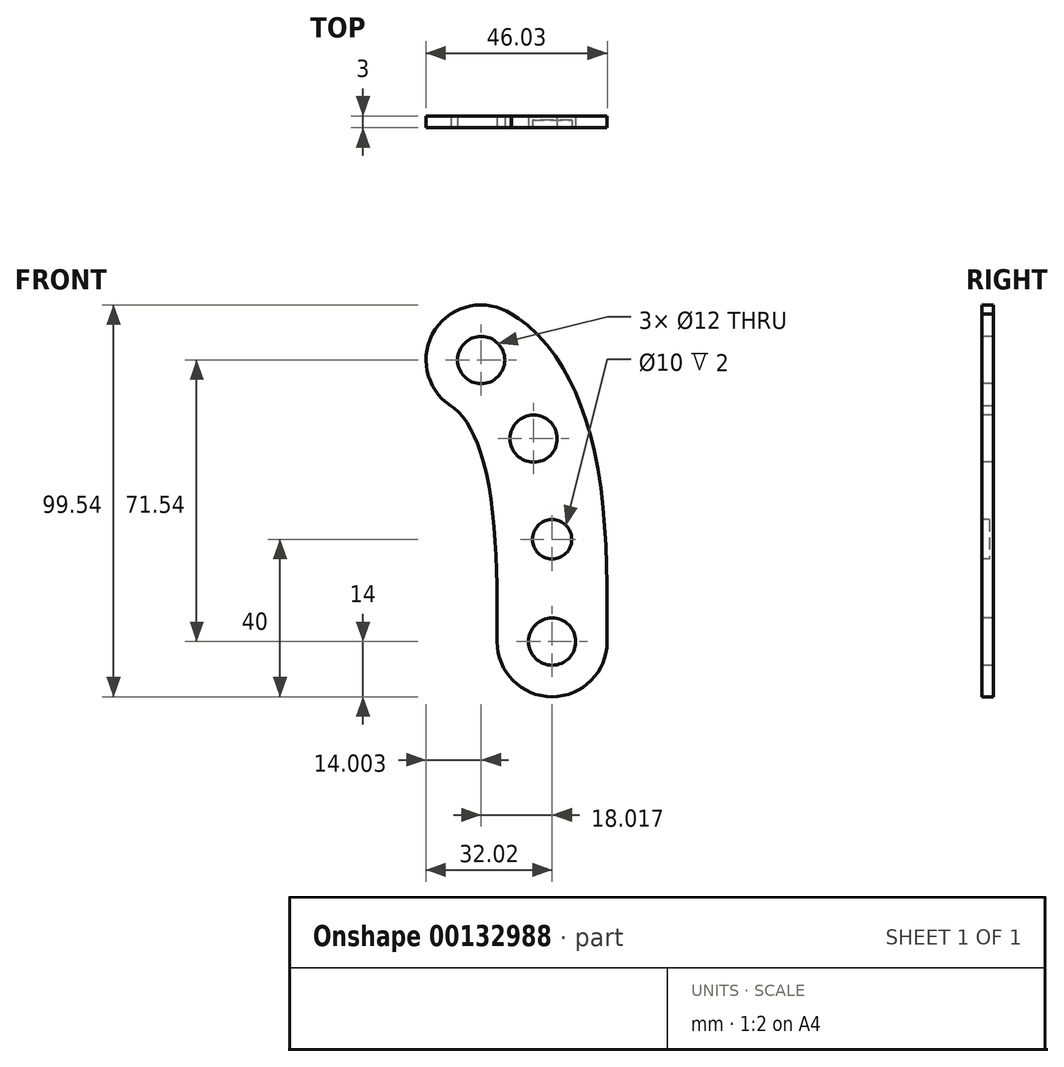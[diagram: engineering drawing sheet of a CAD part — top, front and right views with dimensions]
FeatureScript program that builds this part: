
annotation { "Feature Type Name" : "Feature", "Feature Type Description" : "" }
export const myFeature = defineFeature(function(context is Context, id is Id, definition is map)
    precondition{}
    {
        {
            var Q0;
            Q0=qCreatedBy(makeId("Front.planeOp"),FACE);
            var sketch = newSketch(context, id + "F0", { "sketchPlane" : qUnion([Q0])});
            skCircle(sketch, "E0", {"center": v(18.02, 45.54) * mm, "radius": 6 * mm});
            skCircle(sketch, "E1", {"center": v(4.7, 25.57) * mm, "radius": 6 * mm});
            skCircle(sketch, "E2", {"center": v(0, -26) * mm, "radius": 6 * mm});
            skFitSpline(sketch, "E3", {"points": [v(0, -26) * mm, v(18.02, 45.54) * mm], "startDerivative": vector(0, 78) * mm, "endDerivative": vector(54.05, 35.54) * mm, "construction": true});
            skLineSegment(sketch, "E4.0", {"start": v(-8.67, 29.71) * mm, "end": v(-8.67, 29.71) * mm});
            skArc(sketch, "E5.0", {"start": v(-14, -26) * mm, "mid": v(0, -40) * mm, "end": v(14, -26) * mm});
            skFitSpline(sketch, "E6.0", {"points": [v(14, -26) * mm, v(14, -22.75) * mm, v(14, -16.1) * mm, v(14.2, -6.04) * mm, v(14.8, 3.77) * mm, v(15.94, 12.9) * mm, v(17.44, 19.57) * mm, v(18.94, 24.08) * mm, v(20.19, 27) * mm, v(21.52, 29.42) * mm, v(22.9, 31.34) * mm, v(24.28, 32.8) * mm, v(25.22, 33.52) * mm, v(25.7, 33.84) * mm]});
            skFitSpline(sketch, "E7.0", {"points": [v(-14, -26) * mm, v(-14, -22.75) * mm, v(-14, -15.91) * mm, v(-13.78, -5) * mm, v(-13.11, 6.2) * mm, v(-11.72, 17.47) * mm, v(-9.7, 26.7) * mm, v(-7.32, 33.89) * mm, v(-5.09, 39.15) * mm, v(-2.31, 44.24) * mm, v(1.12, 49.07) * mm, v(5.28, 53.5) * mm, v(8.56, 56.08) * mm, v(10.32, 57.24) * mm]});
            skArc(sketch, "E8.trimOffspring", {"start": v(25.7, 33.84) * mm, "mid": v(29.71, 53.23) * mm, "end": v(10.32, 57.24) * mm});
            skLineSegment(sketch, "E9.trimOffspring", {"start": v(18.08, 21.43) * mm, "end": v(18.08, 21.43) * mm});
            skPoint(sketch, "E10", {"position": v(-13.46, 0) * mm});
            skSolve(sketch);
        }
        {
            var Q0;
            Q0=makeQuery(id+"F0.imprint","IMPRINT",FACE,{"disambiguationData":[TD([[makeQuery(id+"F0.imprint","IMPRINT",EDGE,{"derivedFrom":sQuery(id+"F0.wireOp",EDGE,"E0")}),-1.0]])]});
            extrude(context, id + "F1", {"entities" : qUnion([Q0]), "depth" : 3 * mm});
        }
        {
            var Q0;
            Q0=makeQuery(id+"F1.opExtrude","SWEPT_BODY",BODY,{"disambiguationData":[OSD([sQuery(id+"F0.wireOp",EDGE,"Sjf7detk-OeFK-TYrE-BgNc-QToHNdDsGX7T"),sQuery(id+"F0.wireOp",EDGE,"E0"),sQuery(id+"F0.wireOp",EDGE,"E1"),sQuery(id+"F0.wireOp",EDGE,"E2"),sQuery(id+"F0.wireOp",EDGE,"E5.0"),sQuery(id+"F0.wireOp",EDGE,"E6.0"),sQuery(id+"F0.wireOp",EDGE,"E7.0"),sQuery(id+"F0.wireOp",EDGE,"E8.trimOffspring")])]});
            transform(context, id + "F2", {"entities" : qUnion([Q0]), "transformType" : TransformType.TRANSLATION_3D, "dx" : 50.9 * mm, "dy" : 0 * mm, "dz" : 0 * mm, "makeCopy" : true});
        }
        {
            var Q0;
            Q0=makeQuery(id+"F2.opPattern","COPY",FACE,{"derivedFrom":makeQuery(id+"F1.opExtrude","CAP_FACE",FACE,{"disambiguationData":[OSD([sQuery(id+"F0.wireOp",EDGE,"E0"),sQuery(id+"F0.wireOp",EDGE,"E1"),sQuery(id+"F0.wireOp",EDGE,"E2"),sQuery(id+"F0.wireOp",EDGE,"E5.0"),sQuery(id+"F0.wireOp",EDGE,"E6.0"),sQuery(id+"F0.wireOp",EDGE,"E7.0"),sQuery(id+"F0.wireOp",EDGE,"E8.trimOffspring")])],"isStart":false}),"instanceName":"1"});
            var sketch = newSketch(context, id + "F3", { "sketchPlane" : qUnion([Q0])});
            skCircle(sketch, "E11", {"center": v(50.9, 0) * mm, "radius": 5.5 * mm});
            skPoint(sketch, "E12", {"position": v(37.44, 0) * mm});
            skSolve(sketch);
        }
        {
            var Q0;
            Q0=makeQuery(id+"F3.imprint","IMPRINT",FACE,{"disambiguationData":[TD([[makeQuery(id+"F3.imprint","IMPRINT",EDGE,{"derivedFrom":sQuery(id+"F3.wireOp",EDGE,"E11")}),1.0]])]});
            extrude(context, id + "F4", {"entities" : qUnion([Q0]), "operationType" : NewBodyOperationType.REMOVE, "oppositeDirection" : true, "depth" : 2 * mm});
        }
        {
            var Q0;
            Q0=makeQuery(id+"F1.opExtrude","CAP_FACE",FACE,{"disambiguationData":[OSD([sQuery(id+"F0.wireOp",EDGE,"E0"),sQuery(id+"F0.wireOp",EDGE,"E1"),sQuery(id+"F0.wireOp",EDGE,"E2"),sQuery(id+"F0.wireOp",EDGE,"E5.0"),sQuery(id+"F0.wireOp",EDGE,"E6.0"),sQuery(id+"F0.wireOp",EDGE,"E7.0"),sQuery(id+"F0.wireOp",EDGE,"E8.trimOffspring")])],"isStart":true});
            var sketch = newSketch(context, id + "F5", { "sketchPlane" : qUnion([Q0])});
            skCircle(sketch, "E13", {"center": v(0, 0) * mm, "radius": 5 * mm});
            skSolve(sketch);
        }
        {
            var Q0;
            Q0=makeQuery(id+"F5.imprint","IMPRINT",FACE,{"disambiguationData":[TD([[makeQuery(id+"F5.imprint","IMPRINT",EDGE,{"derivedFrom":sQuery(id+"F5.wireOp",EDGE,"E13")}),1.0]])]});
            extrude(context, id + "F6", {"entities" : qUnion([Q0]), "operationType" : NewBodyOperationType.REMOVE, "oppositeDirection" : true, "depth" : 2 * mm});
        }
        {
            var Q0;
            Q0=makeQuery(id+"F2.opPattern","COPY",BODY,{"derivedFrom":makeQuery(id+"F1.opExtrude","SWEPT_BODY",BODY,{"disambiguationData":[OSD([sQuery(id+"F0.wireOp",EDGE,"E0"),sQuery(id+"F0.wireOp",EDGE,"E1"),sQuery(id+"F0.wireOp",EDGE,"E2"),sQuery(id+"F0.wireOp",EDGE,"E5.0"),sQuery(id+"F0.wireOp",EDGE,"E6.0"),sQuery(id+"F0.wireOp",EDGE,"E7.0"),sQuery(id+"F0.wireOp",EDGE,"E8.trimOffspring")])]}),"instanceName":"1"});
            deleteBodies(context, id + "F7", {"entities" : qUnion([Q0])});
        }
        {
            var Q0;
            Q0=qCreatedBy(makeId("Front.planeOp"),FACE);
            var sketch = newSketch(context, id + "F8", { "sketchPlane" : qUnion([Q0])});
            skLineSegment(sketch, "E14", {"start": v(0, 75.23) * mm, "end": v(0, -64.28) * mm, "construction": true});
            skSolve(sketch);
        }
        {
            var Q0;
            Q0=makeQuery(id+"F1.opExtrude","SWEPT_BODY",BODY,{"disambiguationData":[OSD([sQuery(id+"F0.wireOp",EDGE,"E0"),sQuery(id+"F0.wireOp",EDGE,"E1"),sQuery(id+"F0.wireOp",EDGE,"E2"),sQuery(id+"F0.wireOp",EDGE,"E5.0"),sQuery(id+"F0.wireOp",EDGE,"E6.0"),sQuery(id+"F0.wireOp",EDGE,"E7.0"),sQuery(id+"F0.wireOp",EDGE,"E8.trimOffspring")])]});
            var Q1;
            Q1=sQuery(id+"F8.wireOp",EDGE,"E14");
            transform(context, id + "F9", {"entities" : qUnion([Q0]), "transformType" : TransformType.ROTATION, "transformAxis" : qUnion([Q1]), "angle" : 180 * degree, "makeCopy" : false});
        }
    });
